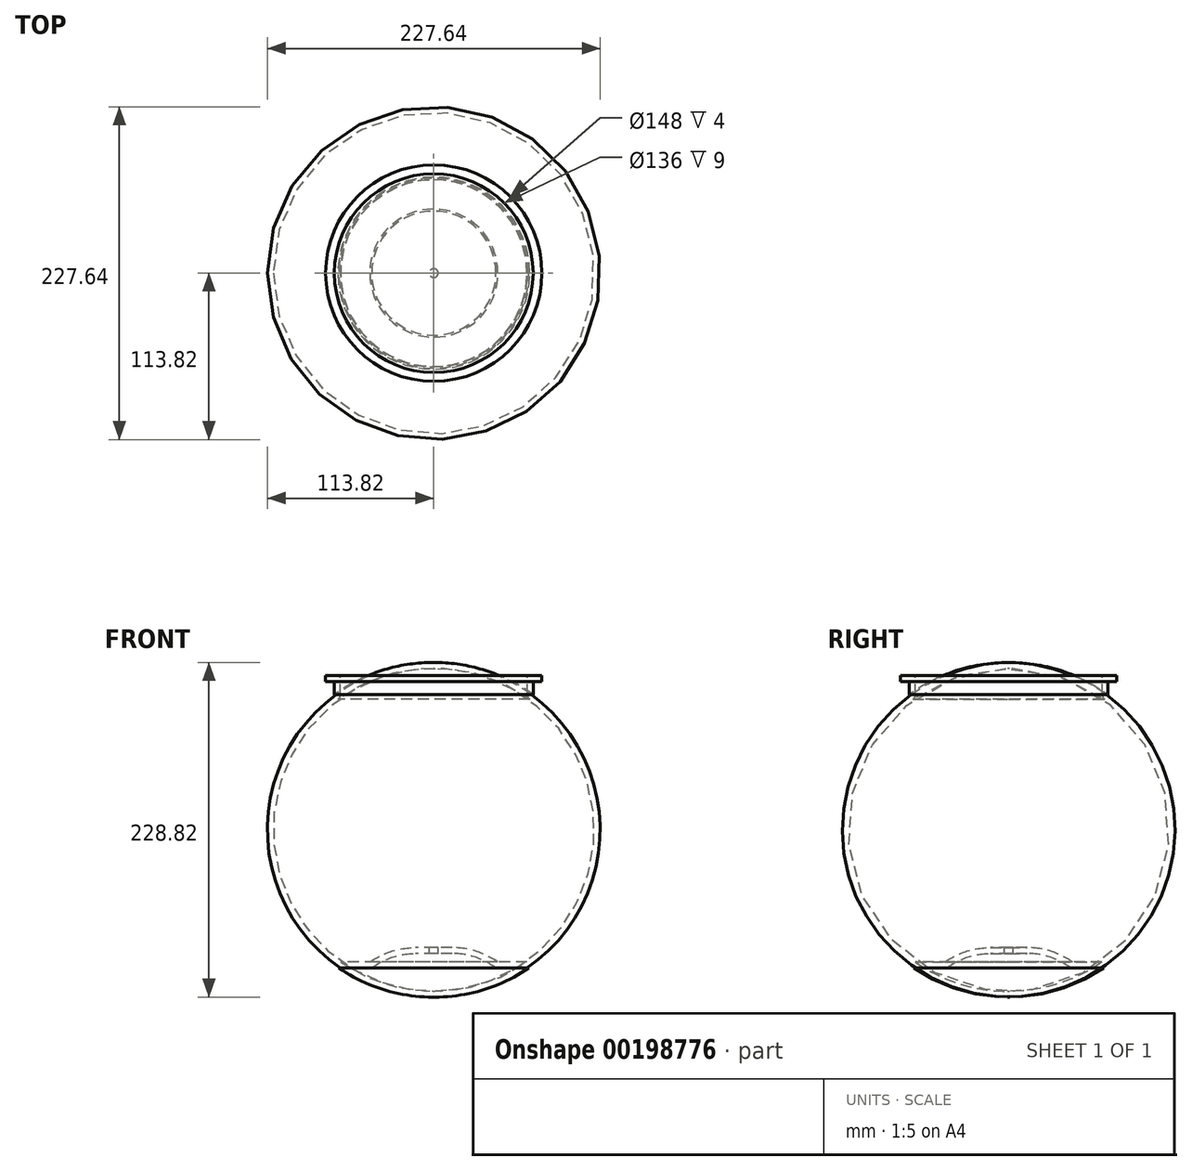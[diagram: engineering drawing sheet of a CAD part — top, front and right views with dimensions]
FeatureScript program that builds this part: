
annotation { "Feature Type Name" : "Feature", "Feature Type Description" : "" }
export const myFeature = defineFeature(function(context is Context, id is Id, definition is map)
    precondition{}
    {
        {
            var Q0;
            Q0=qCreatedBy(makeId("Front.planeOp"),FACE);
            var sketch = newSketch(context, id + "F0", { "sketchPlane" : qUnion([Q0])});
            skLineSegment(sketch, "E0", {"start": v(0, 0) * mm, "end": v(0, 200) * mm, "construction": true});
            skLineSegment(sketch, "E1", {"start": v(0, 10) * mm, "end": v(-12.5, 10) * mm});
            skLineSegment(sketch, "E2", {"start": v(-42.5, 0) * mm, "end": v(-65, 0) * mm});
            skArc(sketch, "E3", {"start": v(-12.5, 10) * mm, "mid": v(-28.31, 7.43) * mm, "end": v(-42.5, 0) * mm});
            skLineSegment(sketch, "E4", {"start": v(0, 200) * mm, "end": v(-74, 200) * mm, "construction": true});
            skLineSegment(sketch, "E5", {"start": v(-74, 200) * mm, "end": v(-64, 200) * mm});
            skLineSegment(sketch, "E6", {"start": v(-64, 200) * mm, "end": v(-64, 187) * mm});
            skLineSegment(sketch, "E7.0", {"start": v(-68, 196) * mm, "end": v(-68, 187) * mm});
            skLineSegment(sketch, "E7.1", {"start": v(-74, 196) * mm, "end": v(-68, 196) * mm});
            skLineSegment(sketch, "E8", {"start": v(-74, 200) * mm, "end": v(-74, 196) * mm});
            skLineSegment(sketch, "E9", {"start": v(-64, 187) * mm, "end": v(-68, 187) * mm, "construction": true});
            skArc(sketch, "E10", {"start": v(-68, 187) * mm, "mid": v(-114.99, 92.72) * mm, "end": v(-65, 0) * mm});
            skArc(sketch, "E11.0", {"start": v(-65.64, 183.77) * mm, "mid": v(-111, 93.4) * mm, "end": v(-63.76, 4) * mm});
            skLineSegment(sketch, "E11.1", {"start": v(-43.8, 4) * mm, "end": v(-63.76, 4) * mm});
            skArc(sketch, "E11.2", {"start": v(-12.5, 14) * mm, "mid": v(-28.93, 11.44) * mm, "end": v(-43.8, 4) * mm});
            skLineSegment(sketch, "E11.3", {"start": v(0, 14) * mm, "end": v(-12.5, 14) * mm});
            skLineSegment(sketch, "E12", {"start": v(0, 14) * mm, "end": v(0, 10) * mm});
            skPoint(sketch, "E13.newPointB", {"position": v(-64, 187) * mm});
            skArc(sketch, "E13.filletArc", {"start": v(-65.64, 183.77) * mm, "mid": v(-64.43, 185.19) * mm, "end": v(-64, 187) * mm});
            skSolve(sketch);
        }
        {
            var Q0;
            Q0 = qSketchRegion(id + "F0", true);
            var Q1;
            Q1=sQuery(id+"F0.wireOp",EDGE,"E12");
            revolve(context, id + "F1", {"entities" : qUnion([Q0]), "axis" : qUnion([Q1]), "revolveType" : RevolveType.FULL});
        }
        {
            var Q0;
            Q0=makeQuery(id+"F1.opRevolve","SWEPT_FACE",FACE,{"disambiguationData":[OSD([sQuery(id+"F0.wireOp",EDGE,"E1")])]});
            var sketch = newSketch(context, id + "F2", { "sketchPlane" : qUnion([Q0])});
            skCircle(sketch, "E14", {"center": v(0, 0) * mm, "radius": 3 * mm});
            skSolve(sketch);
        }
        {
            var Q0;
            Q0 = qSketchRegion(id + "F2", true);
            extrude(context, id + "F3", {"entities" : qUnion([Q0]), "operationType" : NewBodyOperationType.REMOVE, "depth" : 25 * mm, "symmetric" : true});
        }
    });
